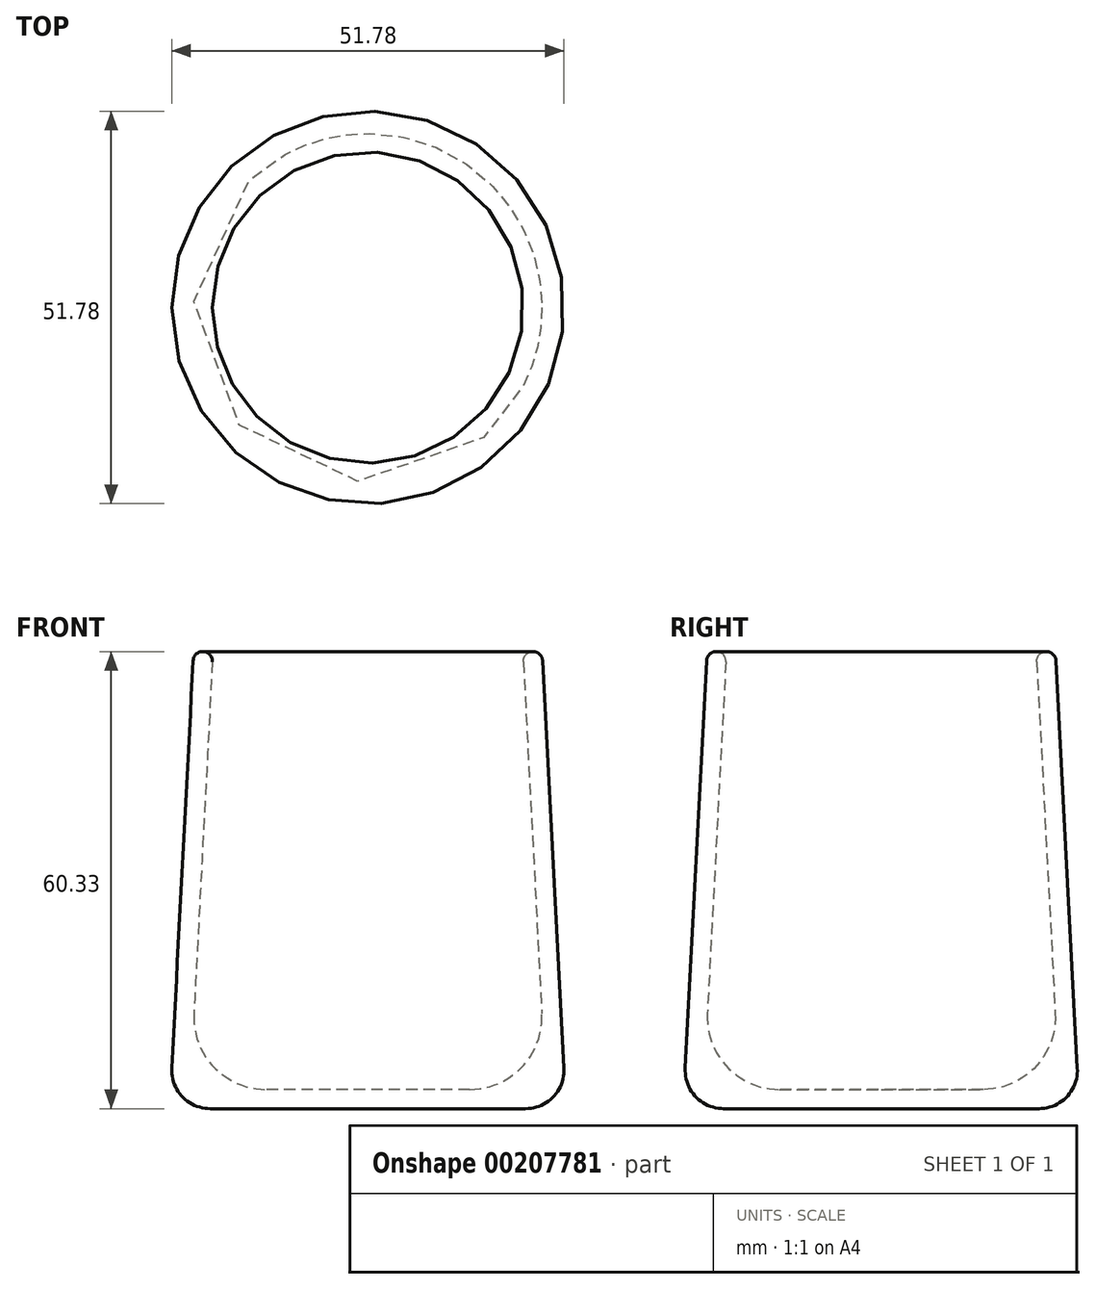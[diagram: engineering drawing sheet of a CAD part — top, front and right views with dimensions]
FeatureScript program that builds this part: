
annotation { "Feature Type Name" : "Feature", "Feature Type Description" : "" }
export const myFeature = defineFeature(function(context is Context, id is Id, definition is map)
    precondition{}
    {
        {
            var Q0;
            Q0=qCreatedBy(makeId("Front.planeOp"),FACE);
            var sketch = newSketch(context, id + "F0", { "sketchPlane" : qUnion([Q0])});
            skLineSegment(sketch, "E0", {"start": v(0, 0) * mm, "end": v(0, 60.33) * mm, "construction": true});
            skLineSegment(sketch, "E1", {"start": v(0, 0) * mm, "end": v(26.16, 0) * mm});
            skLineSegment(sketch, "E2", {"start": v(26.16, 0) * mm, "end": v(23.06, 59.12) * mm});
            skLineSegment(sketch, "E3", {"start": v(23, 60.33) * mm, "end": v(20.46, 60.33) * mm, "construction": true});
            skLineSegment(sketch, "E4", {"start": v(20.53, 58.99) * mm, "end": v(23.49, 2.54) * mm});
            skLineSegment(sketch, "E5", {"start": v(23.49, 2.54) * mm, "end": v(0, 2.54) * mm});
            skLineSegment(sketch, "E6", {"start": v(0, 2.54) * mm, "end": v(0, 0) * mm});
            skArc(sketch, "E7", {"start": v(23.06, 59.12) * mm, "mid": v(21.73, 60.32) * mm, "end": v(20.53, 58.99) * mm});
            skSolve(sketch);
        }
        {
            var Q0;
            Q0=makeQuery(id+"F0.imprint","IMPRINT",FACE,{"disambiguationData":[TD([[makeQuery(id+"F0.imprint","IMPRINT",EDGE,{"derivedFrom":sQuery(id+"F0.wireOp",EDGE,"E1")}),1.0]])]});
            var Q1;
            Q1=sQuery(id+"F0.wireOp",EDGE,"E0");
            revolve(context, id + "F1", {"entities" : qUnion([Q0]), "axis" : qUnion([Q1]), "revolveType" : RevolveType.FULL});
        }
        {
            var Q0;
            Q0=makeQuery(id+"F1.opRevolve","SWEPT_EDGE",EDGE,{"disambiguationData":[OSD([sQuery(id+"F0.wireOp",EDGE,"E4"),sQuery(id+"F0.wireOp",EDGE,"E5")])]});
            fillet(context, id + "F2", {"entities" : qUnion([Q0]), "radius" : 9.52 * mm, "tangentPropagation" : true, "allowEdgeOverflow" : false});
        }
        {
            var Q0;
            Q0=makeQuery(id+"F1.opRevolve","SWEPT_EDGE",EDGE,{"disambiguationData":[OSD([sQuery(id+"F0.wireOp",EDGE,"E1"),sQuery(id+"F0.wireOp",EDGE,"E2")])]});
            fillet(context, id + "F3", {"entities" : qUnion([Q0]), "radius" : 5.08 * mm, "tangentPropagation" : true, "allowEdgeOverflow" : false});
        }
    });
